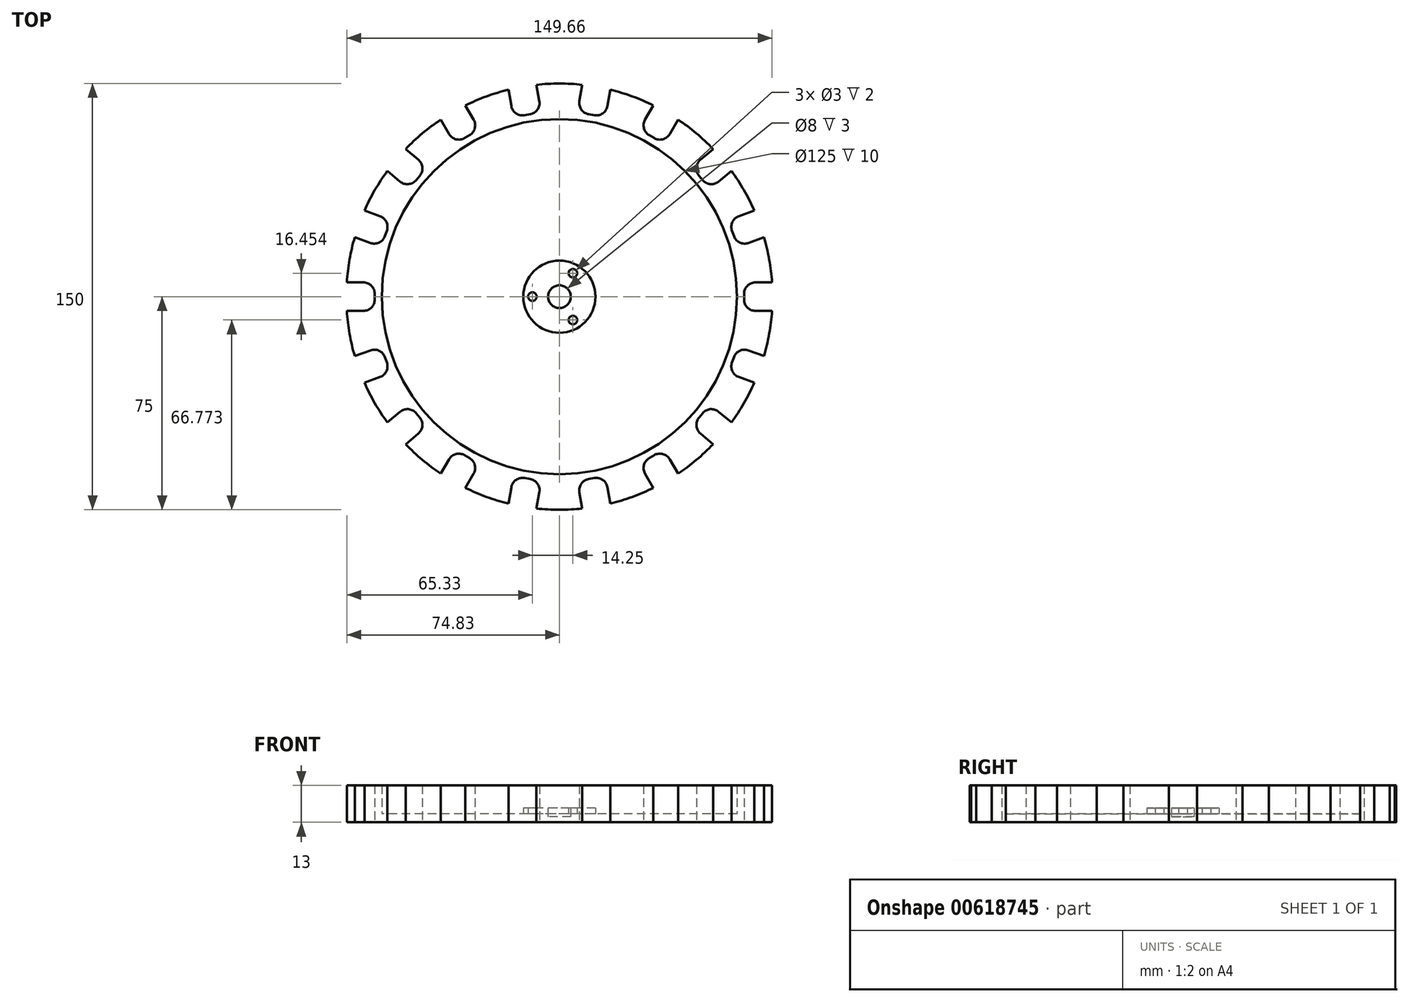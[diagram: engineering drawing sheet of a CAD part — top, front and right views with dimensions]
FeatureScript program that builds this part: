
annotation { "Feature Type Name" : "Feature", "Feature Type Description" : "" }
export const myFeature = defineFeature(function(context is Context, id is Id, definition is map)
    precondition{}
    {
        {
            var Q0;
            Q0=qCreatedBy(makeId("Top.planeOp"),FACE);
            var sketch = newSketch(context, id + "F0", { "sketchPlane" : qUnion([Q0])});
            skCircle(sketch, "E0", {"center": v(0, 0) * mm, "radius": 75 * mm});
            skCircle(sketch, "E1", {"center": v(0, 0) * mm, "radius": 62.5 * mm});
            skLineSegment(sketch, "E2", {"start": v(0, 0) * mm, "end": v(-124.02, 0) * mm, "construction": true});
            skPoint(sketch, "E3", {"position": v(-75, 0) * mm});
            skLineSegment(sketch, "E4.bottom", {"start": v(-75, -5) * mm, "end": v(-69, -5) * mm});
            skLineSegment(sketch, "E4.top", {"start": v(-75, 5) * mm, "end": v(-69, 5) * mm});
            skLineSegment(sketch, "E4.left", {"start": v(-75, -5) * mm, "end": v(-75, 5) * mm});
            skLineSegment(sketch, "E4.right", {"start": v(-65, -1) * mm, "end": v(-65, 1) * mm});
            skPoint(sketch, "E4.middle", {"position": v(-70, 0) * mm});
            skPoint(sketch, "E5.visualSharp", {"position": v(-65, 5) * mm});
            skArc(sketch, "E5.filletArc", {"start": v(-65, 1) * mm, "mid": v(-66.17, 3.83) * mm, "end": v(-69, 5) * mm});
            skPoint(sketch, "E6.visualSharp", {"position": v(-65, -5) * mm});
            skArc(sketch, "E6.filletArc", {"start": v(-69, -5) * mm, "mid": v(-66.17, -3.83) * mm, "end": v(-65, -1) * mm});
            skPoint(sketch, "E7.center", {"position": v(1.56, 0) * mm});
            skCircle(sketch, "E8", {"center": v(0, 0) * mm, "radius": 4 * mm});
            skCircle(sketch, "E9", {"center": v(0, 0) * mm, "radius": 12.7 * mm});
            skCircle(sketch, "E10", {"center": v(0, 0) * mm, "radius": 9.5 * mm, "construction": true});
            skCircle(sketch, "E11", {"center": v(-9.5, 0) * mm, "radius": 1.5 * mm});
            skCircle(sketch, "E12.1.0", {"center": v(-4.75, -8.23) * mm, "radius": 1.5 * mm});
            skCircle(sketch, "E12.2.0", {"center": v(4.75, -8.23) * mm, "radius": 1.5 * mm});
            skCircle(sketch, "E12.3.0", {"center": v(9.5, 0) * mm, "radius": 1.5 * mm});
            skCircle(sketch, "E12.4.0", {"center": v(4.75, 8.23) * mm, "radius": 1.5 * mm});
            skCircle(sketch, "E12.5.0", {"center": v(-4.75, 8.23) * mm, "radius": 1.5 * mm});
            skPoint(sketch, "E13.1.0", {"position": v(-62.8, -17.53) * mm});
            skPoint(sketch, "E13.1.1", {"position": v(-70.48, -25.65) * mm});
            skPoint(sketch, "E13.1.2", {"position": v(-59.37, -26.93) * mm});
            skPoint(sketch, "E13.1.3", {"position": v(-65.78, -23.94) * mm});
            skArc(sketch, "E13.1.4", {"start": v(-63.13, -28.3) * mm, "mid": v(-60.87, -26.23) * mm, "end": v(-60.74, -23.17) * mm});
            skArc(sketch, "E13.1.5", {"start": v(-61.42, -21.3) * mm, "mid": v(-63.5, -19.03) * mm, "end": v(-66.55, -18.9) * mm});
            skLineSegment(sketch, "E13.1.6", {"start": v(-68.77, -30.35) * mm, "end": v(-72.19, -20.95) * mm});
            skLineSegment(sketch, "E13.1.7", {"start": v(-60.74, -23.17) * mm, "end": v(-61.42, -21.3) * mm});
            skLineSegment(sketch, "E13.1.8", {"start": v(-72.19, -20.95) * mm, "end": v(-66.55, -18.9) * mm});
            skLineSegment(sketch, "E13.1.9", {"start": v(-68.77, -30.35) * mm, "end": v(-63.13, -28.3) * mm});
            skPoint(sketch, "E13.2.0", {"position": v(-53, -37.95) * mm});
            skPoint(sketch, "E13.2.1", {"position": v(-57.45, -48.2) * mm});
            skPoint(sketch, "E13.2.2", {"position": v(-46.58, -45.61) * mm});
            skPoint(sketch, "E13.2.3", {"position": v(-53.62, -45) * mm});
            skArc(sketch, "E13.2.4", {"start": v(-49.64, -48.18) * mm, "mid": v(-48.23, -45.47) * mm, "end": v(-49.15, -42.55) * mm});
            skArc(sketch, "E13.2.5", {"start": v(-50.44, -41.02) * mm, "mid": v(-53.15, -39.6) * mm, "end": v(-56.07, -40.52) * mm});
            skLineSegment(sketch, "E13.2.6", {"start": v(-54.24, -52.04) * mm, "end": v(-60.67, -44.38) * mm});
            skLineSegment(sketch, "E13.2.7", {"start": v(-49.15, -42.55) * mm, "end": v(-50.44, -41.02) * mm});
            skLineSegment(sketch, "E13.2.8", {"start": v(-60.67, -44.38) * mm, "end": v(-56.07, -40.52) * mm});
            skLineSegment(sketch, "E13.2.9", {"start": v(-54.24, -52.04) * mm, "end": v(-49.64, -48.18) * mm});
            skPoint(sketch, "E13.3.0", {"position": v(-36.83, -53.8) * mm});
            skPoint(sketch, "E13.3.1", {"position": v(-37.5, -64.95) * mm});
            skPoint(sketch, "E13.3.2", {"position": v(-28.17, -58.8) * mm});
            skPoint(sketch, "E13.3.3", {"position": v(-35, -60.62) * mm});
            skArc(sketch, "E13.3.4", {"start": v(-30.17, -62.26) * mm, "mid": v(-29.77, -59.22) * mm, "end": v(-31.63, -56.8) * mm});
            skArc(sketch, "E13.3.5", {"start": v(-33.37, -55.8) * mm, "mid": v(-36.4, -55.4) * mm, "end": v(-38.83, -57.26) * mm});
            skLineSegment(sketch, "E13.3.6", {"start": v(-33.17, -67.45) * mm, "end": v(-41.83, -62.45) * mm});
            skLineSegment(sketch, "E13.3.7", {"start": v(-31.63, -56.8) * mm, "end": v(-33.37, -55.8) * mm});
            skLineSegment(sketch, "E13.3.8", {"start": v(-41.83, -62.45) * mm, "end": v(-38.83, -57.26) * mm});
            skLineSegment(sketch, "E13.3.9", {"start": v(-33.17, -67.45) * mm, "end": v(-30.17, -62.26) * mm});
            skPoint(sketch, "E13.4.0", {"position": v(-16.21, -63.14) * mm});
            skPoint(sketch, "E13.4.1", {"position": v(-13.02, -73.86) * mm});
            skPoint(sketch, "E13.4.2", {"position": v(-6.36, -64.88) * mm});
            skPoint(sketch, "E13.4.3", {"position": v(-12.16, -68.94) * mm});
            skArc(sketch, "E13.4.4", {"start": v(-7.06, -68.82) * mm, "mid": v(-7.72, -65.83) * mm, "end": v(-10.3, -64.19) * mm});
            skArc(sketch, "E13.4.5", {"start": v(-12.27, -63.84) * mm, "mid": v(-15.26, -64.5) * mm, "end": v(-16.9, -67.08) * mm});
            skLineSegment(sketch, "E13.4.6", {"start": v(-8.1, -74.73) * mm, "end": v(-17.95, -73) * mm});
            skLineSegment(sketch, "E13.4.7", {"start": v(-10.3, -64.19) * mm, "end": v(-12.27, -63.84) * mm});
            skLineSegment(sketch, "E13.4.8", {"start": v(-17.95, -73) * mm, "end": v(-16.9, -67.08) * mm});
            skLineSegment(sketch, "E13.4.9", {"start": v(-8.1, -74.73) * mm, "end": v(-7.06, -68.82) * mm});
            skPoint(sketch, "E13.5.0", {"position": v(6.36, -64.88) * mm});
            skPoint(sketch, "E13.5.1", {"position": v(13.02, -73.86) * mm});
            skPoint(sketch, "E13.5.2", {"position": v(16.21, -63.14) * mm});
            skPoint(sketch, "E13.5.3", {"position": v(12.16, -68.94) * mm});
            skArc(sketch, "E13.5.4", {"start": v(16.9, -67.08) * mm, "mid": v(15.26, -64.5) * mm, "end": v(12.27, -63.84) * mm});
            skArc(sketch, "E13.5.5", {"start": v(10.3, -64.19) * mm, "mid": v(7.72, -65.83) * mm, "end": v(7.06, -68.82) * mm});
            skLineSegment(sketch, "E13.5.6", {"start": v(17.95, -73) * mm, "end": v(8.1, -74.73) * mm});
            skLineSegment(sketch, "E13.5.7", {"start": v(12.27, -63.84) * mm, "end": v(10.3, -64.19) * mm});
            skLineSegment(sketch, "E13.5.8", {"start": v(8.1, -74.73) * mm, "end": v(7.06, -68.82) * mm});
            skLineSegment(sketch, "E13.5.9", {"start": v(17.95, -73) * mm, "end": v(16.9, -67.08) * mm});
            skPoint(sketch, "E13.6.0", {"position": v(28.17, -58.8) * mm});
            skPoint(sketch, "E13.6.1", {"position": v(37.5, -64.95) * mm});
            skPoint(sketch, "E13.6.2", {"position": v(36.83, -53.8) * mm});
            skPoint(sketch, "E13.6.3", {"position": v(35, -60.62) * mm});
            skArc(sketch, "E13.6.4", {"start": v(38.83, -57.26) * mm, "mid": v(36.4, -55.4) * mm, "end": v(33.37, -55.8) * mm});
            skArc(sketch, "E13.6.5", {"start": v(31.63, -56.8) * mm, "mid": v(29.77, -59.22) * mm, "end": v(30.17, -62.26) * mm});
            skLineSegment(sketch, "E13.6.6", {"start": v(41.83, -62.45) * mm, "end": v(33.17, -67.45) * mm});
            skLineSegment(sketch, "E13.6.7", {"start": v(33.37, -55.8) * mm, "end": v(31.63, -56.8) * mm});
            skLineSegment(sketch, "E13.6.8", {"start": v(33.17, -67.45) * mm, "end": v(30.17, -62.26) * mm});
            skLineSegment(sketch, "E13.6.9", {"start": v(41.83, -62.45) * mm, "end": v(38.83, -57.26) * mm});
            skPoint(sketch, "E13.7.0", {"position": v(46.58, -45.61) * mm});
            skPoint(sketch, "E13.7.1", {"position": v(57.45, -48.2) * mm});
            skPoint(sketch, "E13.7.2", {"position": v(53, -37.95) * mm});
            skPoint(sketch, "E13.7.3", {"position": v(53.62, -45) * mm});
            skArc(sketch, "E13.7.4", {"start": v(56.07, -40.52) * mm, "mid": v(53.15, -39.6) * mm, "end": v(50.44, -41.02) * mm});
            skArc(sketch, "E13.7.5", {"start": v(49.15, -42.55) * mm, "mid": v(48.23, -45.47) * mm, "end": v(49.64, -48.18) * mm});
            skLineSegment(sketch, "E13.7.6", {"start": v(60.67, -44.38) * mm, "end": v(54.24, -52.04) * mm});
            skLineSegment(sketch, "E13.7.7", {"start": v(50.44, -41.02) * mm, "end": v(49.15, -42.55) * mm});
            skLineSegment(sketch, "E13.7.8", {"start": v(54.24, -52.04) * mm, "end": v(49.64, -48.18) * mm});
            skLineSegment(sketch, "E13.7.9", {"start": v(60.67, -44.38) * mm, "end": v(56.07, -40.52) * mm});
            skPoint(sketch, "E13.8.0", {"position": v(59.37, -26.93) * mm});
            skPoint(sketch, "E13.8.1", {"position": v(70.48, -25.65) * mm});
            skPoint(sketch, "E13.8.2", {"position": v(62.8, -17.53) * mm});
            skPoint(sketch, "E13.8.3", {"position": v(65.78, -23.94) * mm});
            skArc(sketch, "E13.8.4", {"start": v(66.55, -18.9) * mm, "mid": v(63.5, -19.03) * mm, "end": v(61.42, -21.3) * mm});
            skArc(sketch, "E13.8.5", {"start": v(60.74, -23.17) * mm, "mid": v(60.87, -26.23) * mm, "end": v(63.13, -28.3) * mm});
            skLineSegment(sketch, "E13.8.6", {"start": v(72.19, -20.95) * mm, "end": v(68.77, -30.35) * mm});
            skLineSegment(sketch, "E13.8.7", {"start": v(61.42, -21.3) * mm, "end": v(60.74, -23.17) * mm});
            skLineSegment(sketch, "E13.8.8", {"start": v(68.77, -30.35) * mm, "end": v(63.13, -28.3) * mm});
            skLineSegment(sketch, "E13.8.9", {"start": v(72.19, -20.95) * mm, "end": v(66.55, -18.9) * mm});
            skPoint(sketch, "E13.9.0", {"position": v(65, -5) * mm});
            skPoint(sketch, "E13.9.1", {"position": v(75, 0) * mm});
            skPoint(sketch, "E13.9.2", {"position": v(65, 5) * mm});
            skPoint(sketch, "E13.9.3", {"position": v(70, 0) * mm});
            skArc(sketch, "E13.9.4", {"start": v(69, 5) * mm, "mid": v(66.17, 3.83) * mm, "end": v(65, 1) * mm});
            skArc(sketch, "E13.9.5", {"start": v(65, -1) * mm, "mid": v(66.17, -3.83) * mm, "end": v(69, -5) * mm});
            skLineSegment(sketch, "E13.9.6", {"start": v(75, 5) * mm, "end": v(75, -5) * mm});
            skLineSegment(sketch, "E13.9.7", {"start": v(65, 1) * mm, "end": v(65, -1) * mm});
            skLineSegment(sketch, "E13.9.8", {"start": v(75, -5) * mm, "end": v(69, -5) * mm});
            skLineSegment(sketch, "E13.9.9", {"start": v(75, 5) * mm, "end": v(69, 5) * mm});
            skPoint(sketch, "E13.10.0", {"position": v(62.8, 17.53) * mm});
            skPoint(sketch, "E13.10.1", {"position": v(70.48, 25.65) * mm});
            skPoint(sketch, "E13.10.2", {"position": v(59.37, 26.93) * mm});
            skPoint(sketch, "E13.10.3", {"position": v(65.78, 23.94) * mm});
            skArc(sketch, "E13.10.4", {"start": v(63.13, 28.3) * mm, "mid": v(60.87, 26.23) * mm, "end": v(60.74, 23.17) * mm});
            skArc(sketch, "E13.10.5", {"start": v(61.42, 21.3) * mm, "mid": v(63.5, 19.03) * mm, "end": v(66.55, 18.9) * mm});
            skLineSegment(sketch, "E13.10.6", {"start": v(68.77, 30.35) * mm, "end": v(72.19, 20.95) * mm});
            skLineSegment(sketch, "E13.10.7", {"start": v(60.74, 23.17) * mm, "end": v(61.42, 21.3) * mm});
            skLineSegment(sketch, "E13.10.8", {"start": v(72.19, 20.95) * mm, "end": v(66.55, 18.9) * mm});
            skLineSegment(sketch, "E13.10.9", {"start": v(68.77, 30.35) * mm, "end": v(63.13, 28.3) * mm});
            skPoint(sketch, "E13.11.0", {"position": v(53, 37.95) * mm});
            skPoint(sketch, "E13.11.1", {"position": v(57.45, 48.2) * mm});
            skPoint(sketch, "E13.11.2", {"position": v(46.58, 45.61) * mm});
            skPoint(sketch, "E13.11.3", {"position": v(53.62, 45) * mm});
            skArc(sketch, "E13.11.4", {"start": v(49.64, 48.18) * mm, "mid": v(48.23, 45.47) * mm, "end": v(49.15, 42.55) * mm});
            skArc(sketch, "E13.11.5", {"start": v(50.44, 41.02) * mm, "mid": v(53.15, 39.6) * mm, "end": v(56.07, 40.52) * mm});
            skLineSegment(sketch, "E13.11.6", {"start": v(54.24, 52.04) * mm, "end": v(60.67, 44.38) * mm});
            skLineSegment(sketch, "E13.11.7", {"start": v(49.15, 42.55) * mm, "end": v(50.44, 41.02) * mm});
            skLineSegment(sketch, "E13.11.8", {"start": v(60.67, 44.38) * mm, "end": v(56.07, 40.52) * mm});
            skLineSegment(sketch, "E13.11.9", {"start": v(54.24, 52.04) * mm, "end": v(49.64, 48.18) * mm});
            skPoint(sketch, "E13.12.0", {"position": v(36.83, 53.8) * mm});
            skPoint(sketch, "E13.12.1", {"position": v(37.5, 64.95) * mm});
            skPoint(sketch, "E13.12.2", {"position": v(28.17, 58.8) * mm});
            skPoint(sketch, "E13.12.3", {"position": v(35, 60.62) * mm});
            skArc(sketch, "E13.12.4", {"start": v(30.17, 62.26) * mm, "mid": v(29.77, 59.22) * mm, "end": v(31.63, 56.8) * mm});
            skArc(sketch, "E13.12.5", {"start": v(33.37, 55.8) * mm, "mid": v(36.4, 55.4) * mm, "end": v(38.83, 57.26) * mm});
            skLineSegment(sketch, "E13.12.6", {"start": v(33.17, 67.45) * mm, "end": v(41.83, 62.45) * mm});
            skLineSegment(sketch, "E13.12.7", {"start": v(31.63, 56.8) * mm, "end": v(33.37, 55.8) * mm});
            skLineSegment(sketch, "E13.12.8", {"start": v(41.83, 62.45) * mm, "end": v(38.83, 57.26) * mm});
            skLineSegment(sketch, "E13.12.9", {"start": v(33.17, 67.45) * mm, "end": v(30.17, 62.26) * mm});
            skPoint(sketch, "E13.13.0", {"position": v(16.21, 63.14) * mm});
            skPoint(sketch, "E13.13.1", {"position": v(13.02, 73.86) * mm});
            skPoint(sketch, "E13.13.2", {"position": v(6.36, 64.88) * mm});
            skPoint(sketch, "E13.13.3", {"position": v(12.16, 68.94) * mm});
            skArc(sketch, "E13.13.4", {"start": v(7.06, 68.82) * mm, "mid": v(7.72, 65.83) * mm, "end": v(10.3, 64.19) * mm});
            skArc(sketch, "E13.13.5", {"start": v(12.27, 63.84) * mm, "mid": v(15.26, 64.5) * mm, "end": v(16.9, 67.08) * mm});
            skLineSegment(sketch, "E13.13.6", {"start": v(8.1, 74.73) * mm, "end": v(17.95, 73) * mm});
            skLineSegment(sketch, "E13.13.7", {"start": v(10.3, 64.19) * mm, "end": v(12.27, 63.84) * mm});
            skLineSegment(sketch, "E13.13.8", {"start": v(17.95, 73) * mm, "end": v(16.9, 67.08) * mm});
            skLineSegment(sketch, "E13.13.9", {"start": v(8.1, 74.73) * mm, "end": v(7.06, 68.82) * mm});
            skPoint(sketch, "E13.14.0", {"position": v(-6.36, 64.88) * mm});
            skPoint(sketch, "E13.14.1", {"position": v(-13.02, 73.86) * mm});
            skPoint(sketch, "E13.14.2", {"position": v(-16.21, 63.14) * mm});
            skPoint(sketch, "E13.14.3", {"position": v(-12.16, 68.94) * mm});
            skArc(sketch, "E13.14.4", {"start": v(-16.9, 67.08) * mm, "mid": v(-15.26, 64.5) * mm, "end": v(-12.27, 63.84) * mm});
            skArc(sketch, "E13.14.5", {"start": v(-10.3, 64.19) * mm, "mid": v(-7.72, 65.83) * mm, "end": v(-7.06, 68.82) * mm});
            skLineSegment(sketch, "E13.14.6", {"start": v(-17.95, 73) * mm, "end": v(-8.1, 74.73) * mm});
            skLineSegment(sketch, "E13.14.7", {"start": v(-12.27, 63.84) * mm, "end": v(-10.3, 64.19) * mm});
            skLineSegment(sketch, "E13.14.8", {"start": v(-8.1, 74.73) * mm, "end": v(-7.06, 68.82) * mm});
            skLineSegment(sketch, "E13.14.9", {"start": v(-17.95, 73) * mm, "end": v(-16.9, 67.08) * mm});
            skPoint(sketch, "E13.15.0", {"position": v(-28.17, 58.8) * mm});
            skPoint(sketch, "E13.15.1", {"position": v(-37.5, 64.95) * mm});
            skPoint(sketch, "E13.15.2", {"position": v(-36.83, 53.8) * mm});
            skPoint(sketch, "E13.15.3", {"position": v(-35, 60.62) * mm});
            skArc(sketch, "E13.15.4", {"start": v(-38.83, 57.26) * mm, "mid": v(-36.4, 55.4) * mm, "end": v(-33.37, 55.8) * mm});
            skArc(sketch, "E13.15.5", {"start": v(-31.63, 56.8) * mm, "mid": v(-29.77, 59.22) * mm, "end": v(-30.17, 62.26) * mm});
            skLineSegment(sketch, "E13.15.6", {"start": v(-41.83, 62.45) * mm, "end": v(-33.17, 67.45) * mm});
            skLineSegment(sketch, "E13.15.7", {"start": v(-33.37, 55.8) * mm, "end": v(-31.63, 56.8) * mm});
            skLineSegment(sketch, "E13.15.8", {"start": v(-33.17, 67.45) * mm, "end": v(-30.17, 62.26) * mm});
            skLineSegment(sketch, "E13.15.9", {"start": v(-41.83, 62.45) * mm, "end": v(-38.83, 57.26) * mm});
            skPoint(sketch, "E13.16.0", {"position": v(-46.58, 45.61) * mm});
            skPoint(sketch, "E13.16.1", {"position": v(-57.45, 48.2) * mm});
            skPoint(sketch, "E13.16.2", {"position": v(-53, 37.95) * mm});
            skPoint(sketch, "E13.16.3", {"position": v(-53.62, 45) * mm});
            skArc(sketch, "E13.16.4", {"start": v(-56.07, 40.52) * mm, "mid": v(-53.15, 39.6) * mm, "end": v(-50.44, 41.02) * mm});
            skArc(sketch, "E13.16.5", {"start": v(-49.15, 42.55) * mm, "mid": v(-48.23, 45.47) * mm, "end": v(-49.64, 48.18) * mm});
            skLineSegment(sketch, "E13.16.6", {"start": v(-60.67, 44.38) * mm, "end": v(-54.24, 52.04) * mm});
            skLineSegment(sketch, "E13.16.7", {"start": v(-50.44, 41.02) * mm, "end": v(-49.15, 42.55) * mm});
            skLineSegment(sketch, "E13.16.8", {"start": v(-54.24, 52.04) * mm, "end": v(-49.64, 48.18) * mm});
            skLineSegment(sketch, "E13.16.9", {"start": v(-60.67, 44.38) * mm, "end": v(-56.07, 40.52) * mm});
            skPoint(sketch, "E13.17.0", {"position": v(-59.37, 26.93) * mm});
            skPoint(sketch, "E13.17.1", {"position": v(-70.48, 25.65) * mm});
            skPoint(sketch, "E13.17.2", {"position": v(-62.8, 17.53) * mm});
            skPoint(sketch, "E13.17.3", {"position": v(-65.78, 23.94) * mm});
            skArc(sketch, "E13.17.4", {"start": v(-66.55, 18.9) * mm, "mid": v(-63.5, 19.03) * mm, "end": v(-61.42, 21.3) * mm});
            skArc(sketch, "E13.17.5", {"start": v(-60.74, 23.17) * mm, "mid": v(-60.87, 26.23) * mm, "end": v(-63.13, 28.3) * mm});
            skLineSegment(sketch, "E13.17.6", {"start": v(-72.19, 20.95) * mm, "end": v(-68.77, 30.35) * mm});
            skLineSegment(sketch, "E13.17.7", {"start": v(-61.42, 21.3) * mm, "end": v(-60.74, 23.17) * mm});
            skLineSegment(sketch, "E13.17.8", {"start": v(-68.77, 30.35) * mm, "end": v(-63.13, 28.3) * mm});
            skLineSegment(sketch, "E13.17.9", {"start": v(-72.19, 20.95) * mm, "end": v(-66.55, 18.9) * mm});
            skSolve(sketch);
        }
        {
            var Q0;
            Q0=makeQuery(id+"F0.imprint","IMPRINT",FACE,{"disambiguationData":[TD([[makeQuery(id+"F0.imprint","IMPRINT",EDGE,{"derivedFrom":sQuery(id+"F0.wireOp",EDGE,"E1")}),1.0]])]});
            var Q1;
            Q1=makeQuery(id+"F0.imprint","IMPRINT",FACE,{"disambiguationData":[TD([[makeQuery(id+"F0.imprint","IMPRINT",EDGE,{"derivedFrom":sQuery(id+"F0.wireOp",EDGE,"E8")}),-1.0]])]});
            var Q2;
            Q2=makeQuery(id+"F0.imprint","IMPRINT",FACE,{"disambiguationData":[TD([[makeQuery(id+"F0.imprint","IMPRINT",EDGE,{"derivedFrom":sQuery(id+"F0.wireOp",EDGE,"E12.3.0")}),1.0]])]});
            var Q3;
            Q3=makeQuery(id+"F0.imprint","IMPRINT",FACE,{"disambiguationData":[TD([[makeQuery(id+"F0.imprint","IMPRINT",EDGE,{"derivedFrom":sQuery(id+"F0.wireOp",EDGE,"E12.4.0")}),1.0]])]});
            var Q4;
            Q4=makeQuery(id+"F0.imprint","IMPRINT",FACE,{"disambiguationData":[TD([[makeQuery(id+"F0.imprint","IMPRINT",EDGE,{"derivedFrom":sQuery(id+"F0.wireOp",EDGE,"E12.5.0")}),1.0]])]});
            var Q5;
            Q5=makeQuery(id+"F0.imprint","IMPRINT",FACE,{"disambiguationData":[TD([[makeQuery(id+"F0.imprint","IMPRINT",EDGE,{"derivedFrom":sQuery(id+"F0.wireOp",EDGE,"E11")}),1.0]])]});
            var Q6;
            Q6=makeQuery(id+"F0.imprint","IMPRINT",FACE,{"disambiguationData":[TD([[makeQuery(id+"F0.imprint","IMPRINT",EDGE,{"derivedFrom":sQuery(id+"F0.wireOp",EDGE,"E12.1.0")}),1.0]])]});
            var Q7;
            Q7=makeQuery(id+"F0.imprint","IMPRINT",FACE,{"disambiguationData":[TD([[makeQuery(id+"F0.imprint","IMPRINT",EDGE,{"derivedFrom":sQuery(id+"F0.wireOp",EDGE,"E12.2.0")}),1.0]])]});
            extrude(context, id + "F1", {"entities" : qUnion([Q0, Q1, Q2, Q3, Q4, Q5, Q6, Q7]), "depth" : 3 * mm, "offsetDistance" : 25 * mm});
        }
        {
            var Q0;
            Q0=makeQuery(id+"F0.imprint","IMPRINT",FACE,{"disambiguationData":[TD([[makeQuery(id+"F0.imprint","IMPRINT",EDGE,{"derivedFrom":sQuery(id+"F0.wireOp",EDGE,"E1")}),-1.0]])]});
            extrude(context, id + "F2", {"entities" : qUnion([Q0]), "operationType" : NewBodyOperationType.ADD, "depth" : 13 * mm, "offsetDistance" : 25 * mm});
        }
        {
            var Q0;
            Q0=makeQuery(id+"F0.imprint","IMPRINT",FACE,{"disambiguationData":[TD([[makeQuery(id+"F0.imprint","IMPRINT",EDGE,{"derivedFrom":sQuery(id+"F0.wireOp",EDGE,"E8")}),-1.0]])]});
            var Q1;
            Q1=makeQuery(id+"F0.imprint","IMPRINT",FACE,{"disambiguationData":[TD([[makeQuery(id+"F0.imprint","IMPRINT",EDGE,{"derivedFrom":sQuery(id+"F0.wireOp",EDGE,"E12.5.0")}),1.0]])]});
            var Q2;
            Q2=makeQuery(id+"F0.imprint","IMPRINT",FACE,{"disambiguationData":[TD([[makeQuery(id+"F0.imprint","IMPRINT",EDGE,{"derivedFrom":sQuery(id+"F0.wireOp",EDGE,"E12.3.0")}),1.0]])]});
            var Q3;
            Q3=makeQuery(id+"F0.imprint","IMPRINT",FACE,{"disambiguationData":[TD([[makeQuery(id+"F0.imprint","IMPRINT",EDGE,{"derivedFrom":sQuery(id+"F0.wireOp",EDGE,"E12.1.0")}),1.0]])]});
            extrude(context, id + "F3", {"entities" : qUnion([Q0, Q1, Q2, Q3]), "operationType" : NewBodyOperationType.ADD, "depth" : 5 * mm, "offsetDistance" : 25 * mm});
        }
        {
            var Q0;
            Q0=makeQuery(id+"F0.imprint","IMPRINT",FACE,{"disambiguationData":[TD([[makeQuery(id+"F0.imprint","IMPRINT",EDGE,{"derivedFrom":sQuery(id+"F0.wireOp",EDGE,"E8")}),1.0]])]});
            extrude(context, id + "F4", {"entities" : qUnion([Q0]), "operationType" : NewBodyOperationType.ADD, "depth" : 2 * mm, "offsetDistance" : 25 * mm});
        }
    });
